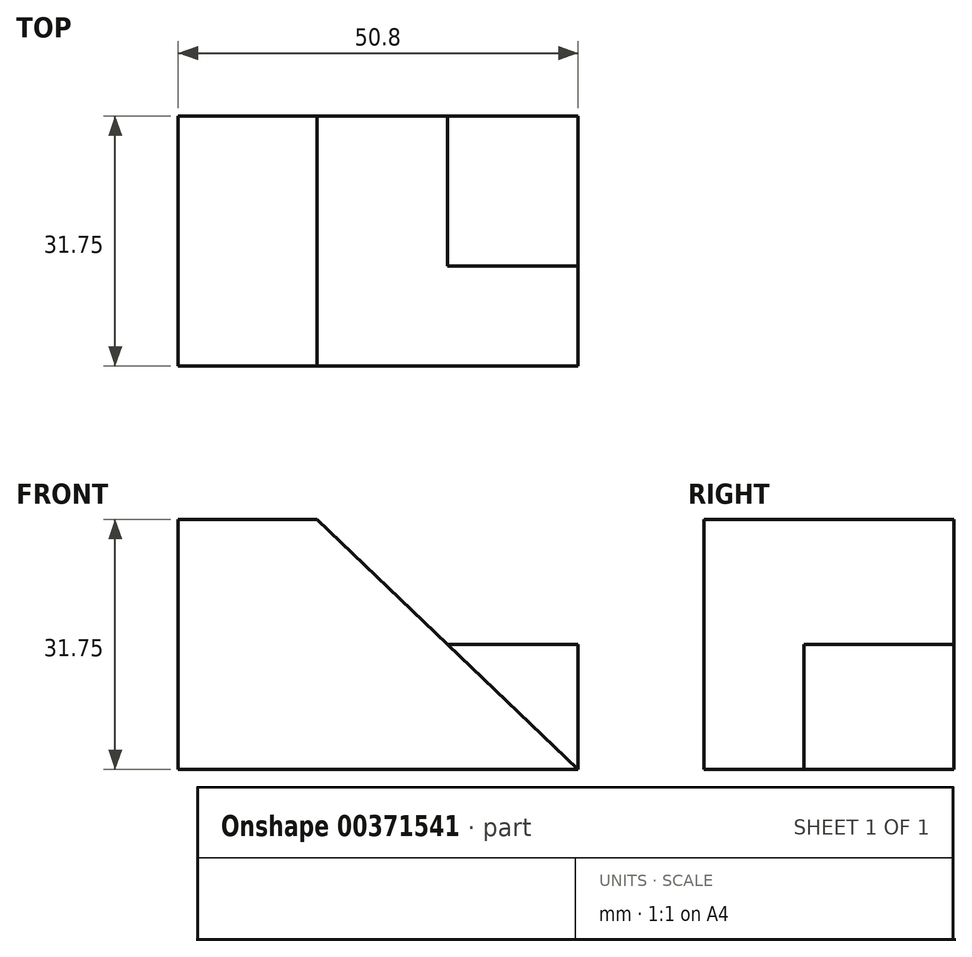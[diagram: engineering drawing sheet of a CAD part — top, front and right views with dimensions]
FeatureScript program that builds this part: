
annotation { "Feature Type Name" : "Feature", "Feature Type Description" : "" }
export const myFeature = defineFeature(function(context is Context, id is Id, definition is map)
    precondition{}
    {
        {
            var Q0;
            Q0=qCreatedBy(makeId("Front.planeOp"),FACE);
            var sketch = newSketch(context, id + "F0", { "sketchPlane" : qUnion([Q0])});
            skLineSegment(sketch, "E0", {"start": v(0, 0) * mm, "end": v(50.8, 0) * mm});
            skLineSegment(sketch, "E1", {"start": v(50.8, 0) * mm, "end": v(50.8, 31.75) * mm});
            skLineSegment(sketch, "E2", {"start": v(50.8, 31.75) * mm, "end": v(0, 31.75) * mm});
            skLineSegment(sketch, "E3", {"start": v(0, 31.75) * mm, "end": v(0, 0) * mm});
            skSolve(sketch);
        }
        {
            var Q0;
            Q0=makeQuery(id+"F0.imprint","IMPRINT",FACE,{"disambiguationData":[TD([[makeQuery(id+"F0.imprint","IMPRINT",EDGE,{"derivedFrom":sQuery(id+"F0.wireOp",EDGE,"E0")}),1.0]])]});
            extrude(context, id + "F1", {"entities" : qUnion([Q0]), "depth" : 31.75 * mm});
        }
        {
            var Q0;
            Q0=makeQuery(id+"F1.opExtrude","CAP_FACE",FACE,{"disambiguationData":[OSD([sQuery(id+"F0.wireOp",EDGE,"E0"),sQuery(id+"F0.wireOp",EDGE,"E1"),sQuery(id+"F0.wireOp",EDGE,"E2"),sQuery(id+"F0.wireOp",EDGE,"E3")])],"isStart":false});
            var sketch = newSketch(context, id + "F2", { "sketchPlane" : qUnion([Q0])});
            skLineSegment(sketch, "E4", {"start": v(17.64, 31.75) * mm, "end": v(50.8, 0) * mm});
            skSolve(sketch);
        }
        {
            var Q0;
            Q0 = qSketchRegion(id + "F2", true);
            var Q1;
            {var subQ0=sQuery(id+"F2.wireOp",EDGE,"E4");Q1=makeQuery(id+"F2.imprint","IMPRINT",FACE,{"disambiguationData":[TD([[makeQuery(id+"F2.imprint","IMPRINT",EDGE,{"derivedFrom":subQ0}),1.0]])]});}
            extrude(context, id + "F3", {"entities" : qUnion([Q0, Q1]), "operationType" : NewBodyOperationType.REMOVE, "oppositeDirection" : true, "depth" : 12.7 * mm});
        }
        {
            var Q0;
            Q0=makeQuery(id+"F3.boolean.opBoolean","COPY",FACE,{"derivedFrom":makeQuery(id+"F3.opExtrude","CAP_FACE",FACE,{"disambiguationData":[OSD([sQuery(id+"F0.wireOp",EDGE,"E1"),sQuery(id+"F0.wireOp",EDGE,"E2"),sQuery(id+"F2.wireOp",EDGE,"E4")])],"isStart":false})});
            var sketch = newSketch(context, id + "F4", { "sketchPlane" : qUnion([Q0])});
            skLineSegment(sketch, "E5", {"start": v(34.22, 15.87) * mm, "end": v(34.22, 31.75) * mm});
            skSolve(sketch);
        }
        {
            var Q0;
            Q0 = qSketchRegion(id + "F4", true);
            var Q1;
            {var subQ0=sQuery(id+"F4.wireOp",EDGE,"E5");Q1=makeQuery(id+"F4.imprint","IMPRINT",FACE,{"disambiguationData":[TD([[makeQuery(id+"F4.imprint","IMPRINT",EDGE,{"derivedFrom":subQ0}),1.0]])]});}
            extrude(context, id + "F5", {"entities" : qUnion([Q0, Q1]), "operationType" : NewBodyOperationType.REMOVE, "oppositeDirection" : true, "depth" : 25.4 * mm});
        }
        {
            var Q0;
            Q0=makeQuery(id+"F3.boolean.opBoolean","COPY",FACE,{"derivedFrom":makeQuery(id+"F3.opExtrude","CAP_FACE",FACE,{"disambiguationData":[OSD([sQuery(id+"F0.wireOp",EDGE,"E1"),sQuery(id+"F0.wireOp",EDGE,"E2"),sQuery(id+"F2.wireOp",EDGE,"E4")])],"isStart":false})});
            var sketch = newSketch(context, id + "F6", { "sketchPlane" : qUnion([Q0])});
            skLineSegment(sketch, "E6", {"start": v(34.22, 23.81) * mm, "end": v(50.8, 23.81) * mm});
            skLineSegment(sketch, "E7", {"start": v(50.8, 23.81) * mm, "end": v(63.04, 31.75) * mm});
            skSolve(sketch);
        }
        {
            var Q0;
            Q0 = qSketchRegion(id + "F6", true);
            var Q1;
            {var subQ0=sQuery(id+"F6.wireOp",EDGE,"E6");Q1=makeQuery(id+"F6.imprint","IMPRINT",FACE,{"disambiguationData":[TD([[makeQuery(id+"F6.imprint","IMPRINT",EDGE,{"derivedFrom":subQ0}),1.0]])]});}
            extrude(context, id + "F7", {"entities" : qUnion([Q0, Q1]), "operationType" : NewBodyOperationType.REMOVE, "oppositeDirection" : true, "depth" : 25.4 * mm});
        }
        {
            var Q0;
            Q0=makeQuery(id+"F3.boolean.opBoolean","COPY",FACE,{"derivedFrom":makeQuery(id+"F3.opExtrude","CAP_FACE",FACE,{"disambiguationData":[OSD([sQuery(id+"F0.wireOp",EDGE,"E1"),sQuery(id+"F0.wireOp",EDGE,"E2"),sQuery(id+"F2.wireOp",EDGE,"E4")])],"isStart":false})});
            var sketch = newSketch(context, id + "F8", { "sketchPlane" : qUnion([Q0])});
            skLineSegment(sketch, "E8", {"start": v(34.22, 15.88) * mm, "end": v(50.8, 15.88) * mm});
            skLineSegment(sketch, "E9", {"start": v(50.8, 15.88) * mm, "end": v(63.6, 23.81) * mm});
            skSolve(sketch);
        }
        {
            var Q0;
            Q0 = qSketchRegion(id + "F8", true);
            var Q1;
            {var subQ0=sQuery(id+"F8.wireOp",EDGE,"E8");Q1=makeQuery(id+"F8.imprint","IMPRINT",FACE,{"disambiguationData":[TD([[makeQuery(id+"F8.imprint","IMPRINT",EDGE,{"derivedFrom":subQ0}),1.0]])]});}
            extrude(context, id + "F9", {"entities" : qUnion([Q0, Q1]), "operationType" : NewBodyOperationType.REMOVE, "oppositeDirection" : true, "depth" : 25.4 * mm});
        }
    });
